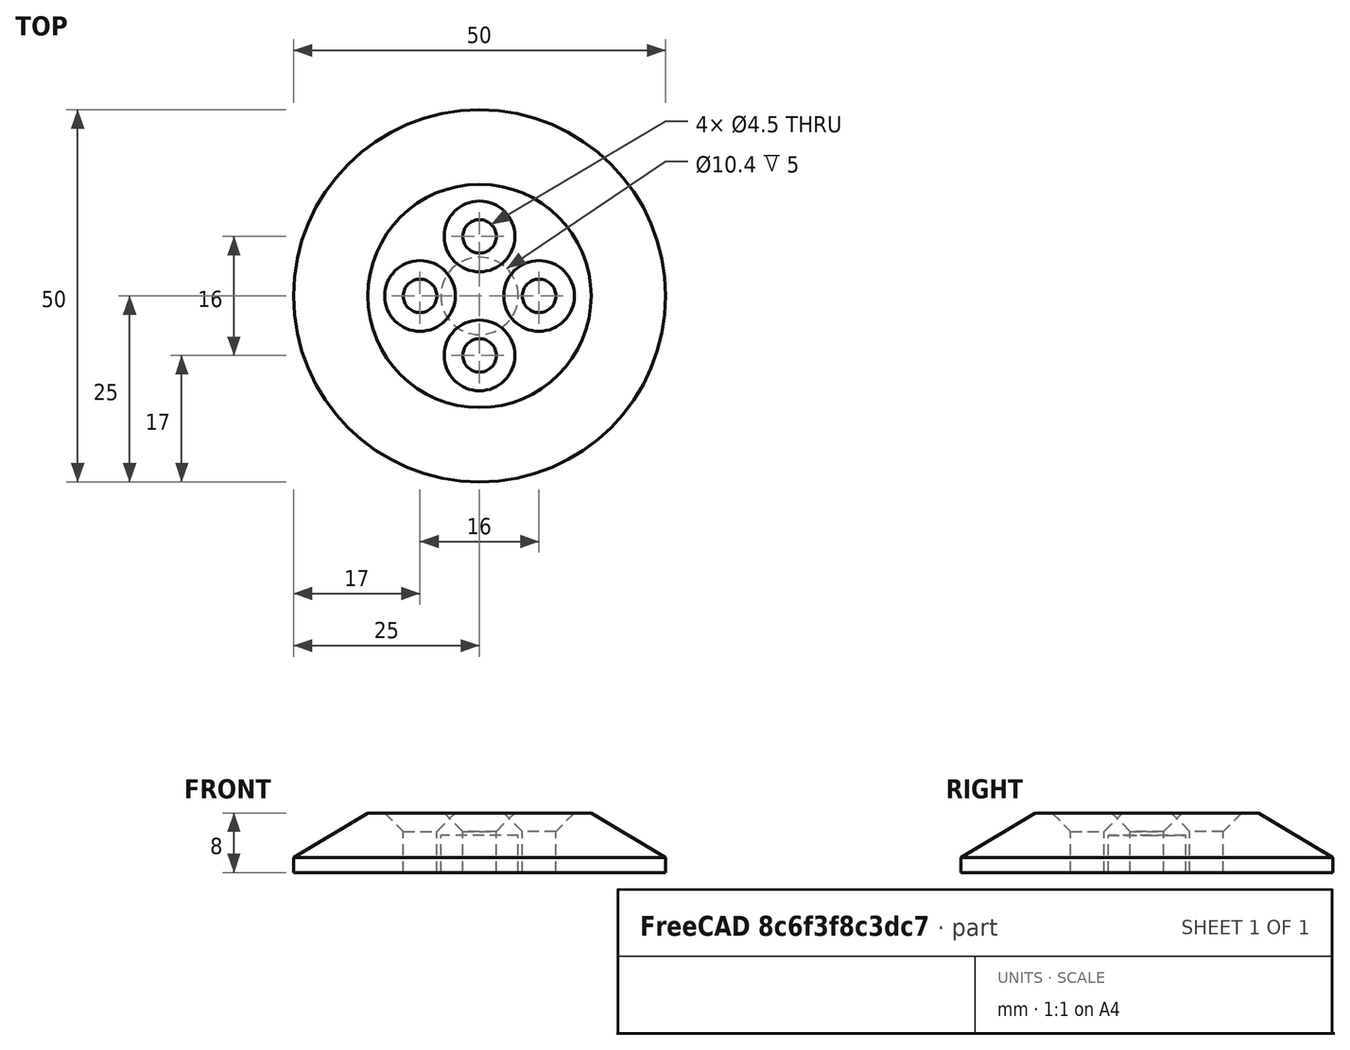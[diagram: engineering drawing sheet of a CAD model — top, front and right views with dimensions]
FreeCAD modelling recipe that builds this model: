
FCSTD DOCUMENT  (FreeCAD 0.17R13541 (Git))
Label: taco_externo_rueda
License: All rights reserved
LicenseURL: http://en.wikipedia.org/wiki/All_rights_reserved
objects: Part::Cylinder×4, Part::MultiFuse×2, Part::FeaturePython×1, Part::Cone×1, Part::Cut×1, Part::Chamfer×1
note: 10 computed .brp shape members not serialized (recipe doc carries the construction recipe); baked Part::Feature solids carry a one-line shape summary decoded from their .brp

FEATURE [Part::Cylinder] Cylinder  label="eje"
  Angle = 360
  AttacherType = Attacher::AttachEngine3D
  Height = 5
  Radius = 5.2
FEATURE [Part::Cylinder] Cylinder001  label="taco"
  Angle = 360
  AttacherType = Attacher::AttachEngine3D
  Height = 8
  Radius = 15
FEATURE [Part::Cylinder] Cylinder002  label="Cilindro"
  Angle = 360
  AttacherType = Attacher::AttachEngine3D
  Height = 15
  Placement = pos=(8,0,0) rot=(0,0,1;0rad)
  Radius = 2.25
FEATURE [Part::FeaturePython] Array  # Draft array (typed FeaturePython)
  Angle = 360
  ArrayType = 1
  Axis = (0,0,1)
  Base = -> Cylinder002
  Center = (0,0,0)
  Fuse = false
  IntervalAxis = (0,0,0)
  IntervalX = (1,0,0)
  IntervalY = (0,1,0)
  IntervalZ = (0,0,0)
  NumberPolar = 4
  NumberX = 2
  NumberY = 2
  NumberZ = 1
FEATURE [Part::Cylinder] Cylinder005  label="Cilindro003"
  Angle = 360
  AttacherType = Attacher::AttachEngine3D
  Height = 2
  Radius = 25
FEATURE [Part::Cone] Cone  label="Cono"
  Angle = 360
  AttacherType = Attacher::AttachEngine3D
  Height = 6
  Placement = pos=(0,0,2) rot=(0,0,1;0rad)
  Radius1 = 25
  Radius2 = 15
FEATURE [Part::MultiFuse] Fusion
  Refine = true
  Shapes = -> [Array,Cylinder]
FEATURE [Part::MultiFuse] Fusion001
  Refine = true
  Shapes = -> [Cylinder001,Cylinder005,Cone]
FEATURE [Part::Cut] Cut
  Base = -> Fusion001
  Refine = true
  Tool = -> Fusion
FEATURE [Part::Chamfer] Chamfer
  Base = -> Cut
  Edges = 4 edges r=2.5: [Edge2,Edge3,Edge4,Edge5]
